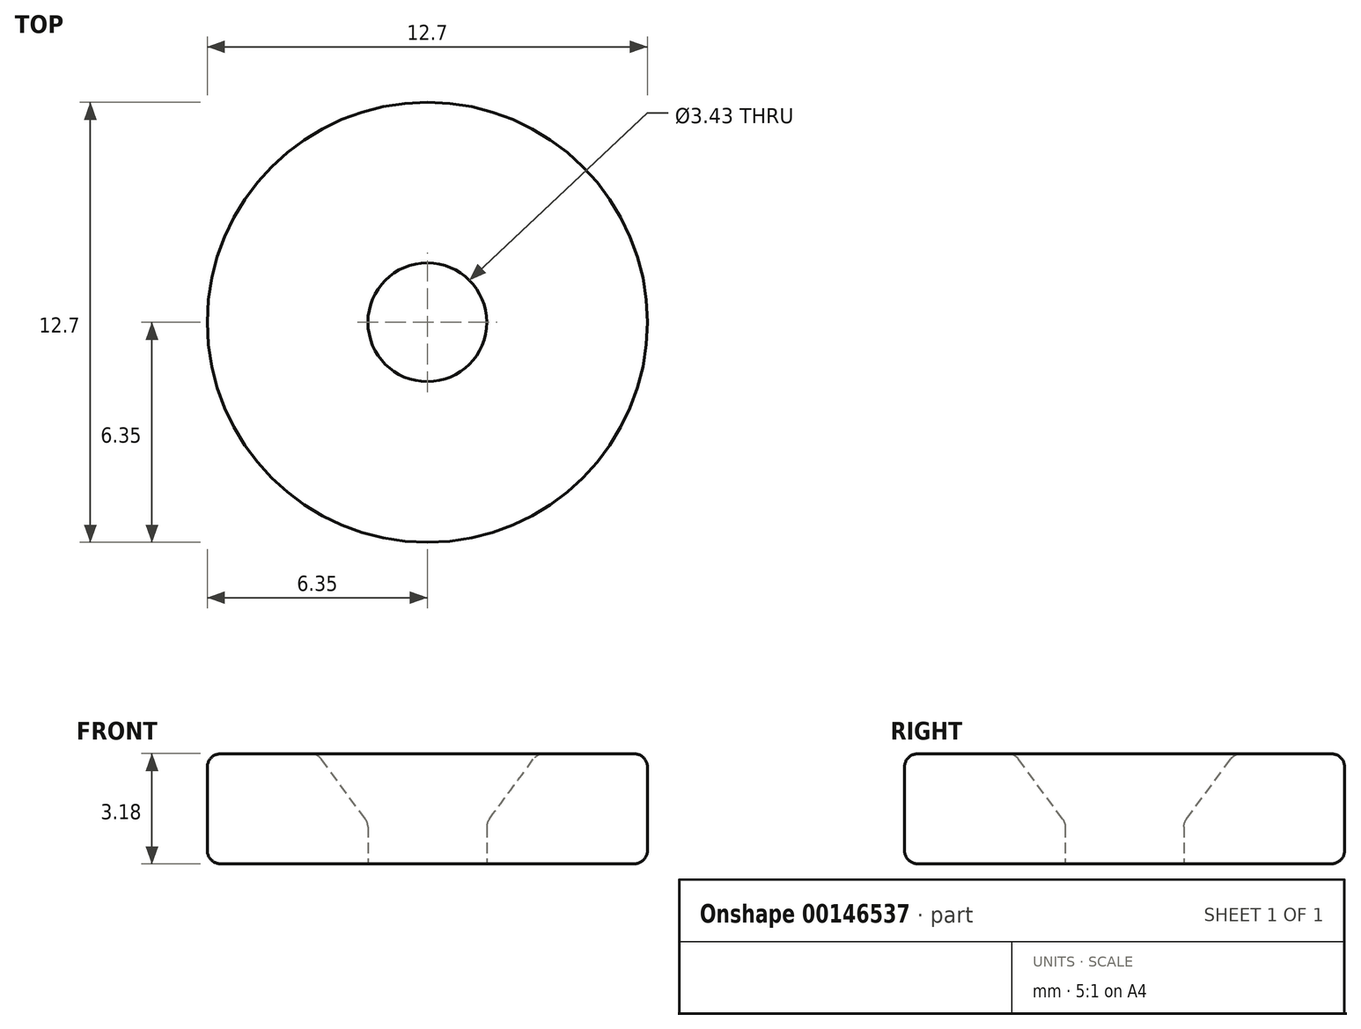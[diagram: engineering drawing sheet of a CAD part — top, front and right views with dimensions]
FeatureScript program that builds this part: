
annotation { "Feature Type Name" : "Feature", "Feature Type Description" : "" }
export const myFeature = defineFeature(function(context is Context, id is Id, definition is map)
    precondition{}
    {
        {
            var Q0;
            Q0=qCreatedBy(makeId("Front.planeOp"),FACE);
            var sketch = newSketch(context, id + "F0", { "sketchPlane" : qUnion([Q0])});
            skLineSegment(sketch, "E0", {"start": v(1.71, 0) * mm, "end": v(6.35, 0) * mm});
            skLineSegment(sketch, "E1", {"start": v(6.35, 0) * mm, "end": v(6.35, 3.18) * mm});
            skLineSegment(sketch, "E2", {"start": v(6.35, 3.18) * mm, "end": v(3.18, 3.18) * mm});
            skLineSegment(sketch, "E3", {"start": v(1.71, 0) * mm, "end": v(1.71, 1.2) * mm});
            skLineSegment(sketch, "E4", {"start": v(1.71, 1.2) * mm, "end": v(3.18, 3.18) * mm});
            skLineSegment(sketch, "E5", {"start": v(0, 0) * mm, "end": v(0, 6.03) * mm, "construction": true});
            skSolve(sketch);
        }
        {
            var Q0;
            Q0=makeQuery(id+"F0.imprint","IMPRINT",FACE,{"disambiguationData":[TD([[makeQuery(id+"F0.imprint","IMPRINT",EDGE,{"derivedFrom":sQuery(id+"F0.wireOp",EDGE,"E0")}),1.0]])]});
            var Q1;
            Q1=sQuery(id+"F0.wireOp",EDGE,"E5");
            revolve(context, id + "F1", {"entities" : qUnion([Q0]), "axis" : qUnion([Q1]), "revolveType" : RevolveType.FULL});
        }
        {
            var Q0;
            Q0=makeQuery(id+"F1.opRevolve","SWEPT_EDGE",EDGE,{"disambiguationData":[OSD([sQuery(id+"F0.wireOp",EDGE,"E2"),sQuery(id+"F0.wireOp",EDGE,"E4")])]});
            var Q1;
            Q1=makeQuery(id+"F1.opRevolve","SWEPT_EDGE",EDGE,{"disambiguationData":[OSD([sQuery(id+"F0.wireOp",EDGE,"E3"),sQuery(id+"F0.wireOp",EDGE,"E4")])]});
            var Q2;
            Q2=makeQuery(id+"F1.opRevolve","SWEPT_EDGE",EDGE,{"disambiguationData":[OSD([sQuery(id+"F0.wireOp",EDGE,"E1"),sQuery(id+"F0.wireOp",EDGE,"E2")])]});
            var Q3;
            Q3=makeQuery(id+"F1.opRevolve","SWEPT_EDGE",EDGE,{"disambiguationData":[OSD([sQuery(id+"F0.wireOp",EDGE,"E0"),sQuery(id+"F0.wireOp",EDGE,"E1")])]});
            fillet(context, id + "F2", {"entities" : qUnion([Q0, Q1, Q2, Q3]), "radius" : 0.38 * mm, "tangentPropagation" : true, "allowEdgeOverflow" : false});
        }
    });
